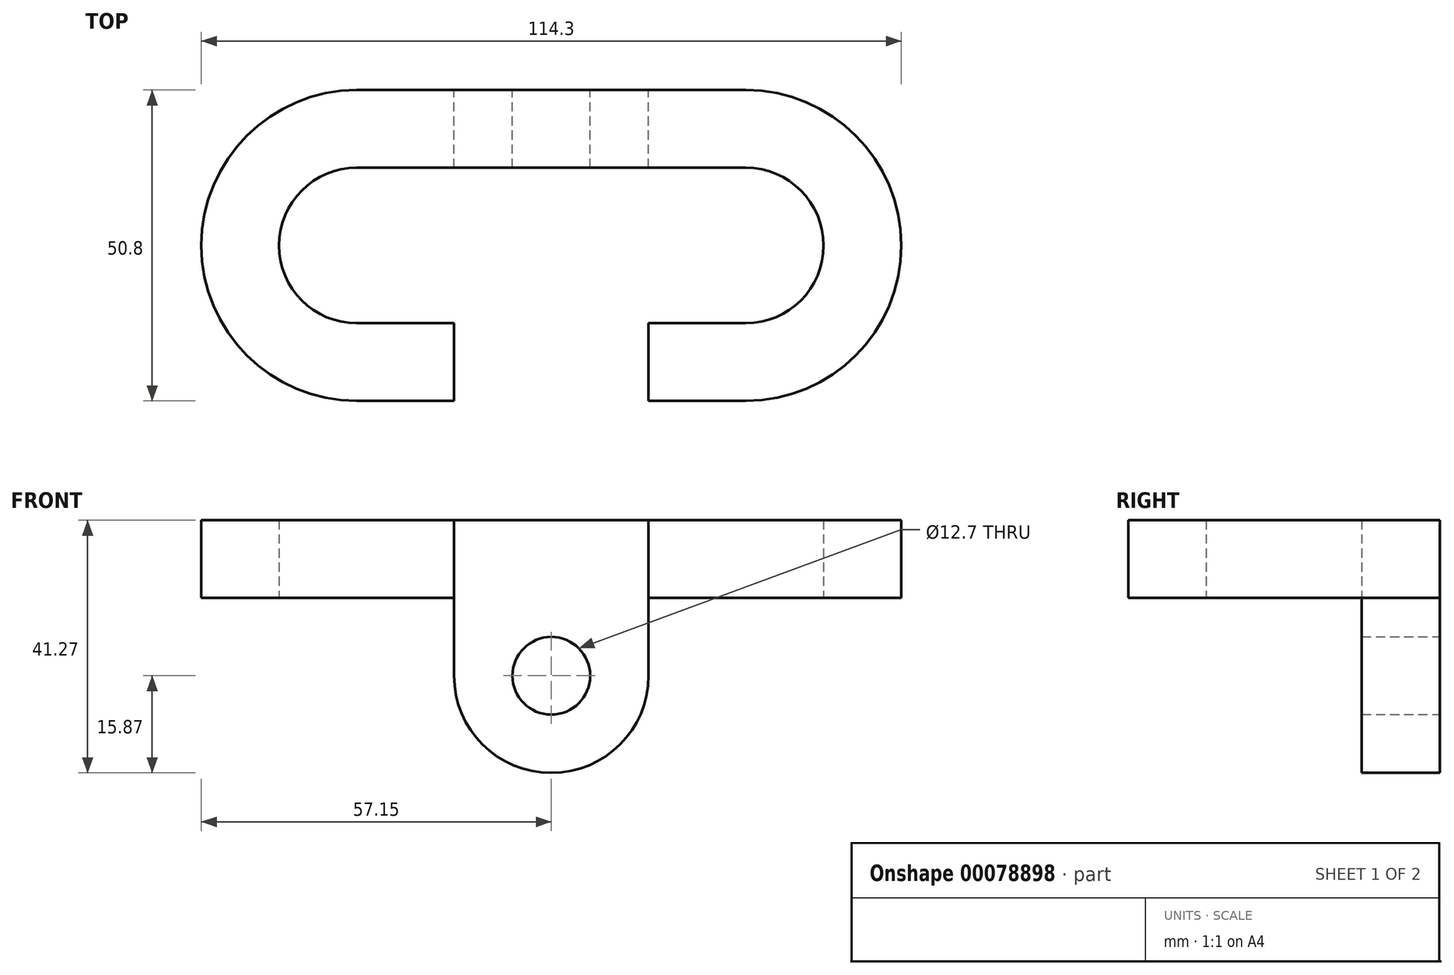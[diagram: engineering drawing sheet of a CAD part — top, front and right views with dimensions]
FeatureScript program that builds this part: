
annotation { "Feature Type Name" : "Feature", "Feature Type Description" : "" }
export const myFeature = defineFeature(function(context is Context, id is Id, definition is map)
    precondition{}
    {
        {
            var Q0;
            Q0=qCreatedBy(makeId("Top.planeOp"),FACE);
            var sketch = newSketch(context, id + "F0", { "sketchPlane" : qUnion([Q0])});
            skCircle(sketch, "E0", {"center": v(0, 0) * mm, "radius": 25.4 * mm});
            skCircle(sketch, "E1", {"center": v(63.5, 0) * mm, "radius": 25.4 * mm});
            skCircle(sketch, "E2", {"center": v(0, 0) * mm, "radius": 12.7 * mm});
            skCircle(sketch, "E3", {"center": v(63.5, 0) * mm, "radius": 12.7 * mm});
            skLineSegment(sketch, "E4", {"start": v(0, 25.4) * mm, "end": v(63.5, 25.4) * mm});
            skLineSegment(sketch, "E5", {"start": v(63.5, 12.7) * mm, "end": v(0, 12.7) * mm});
            skLineSegment(sketch, "E6", {"start": v(0, -25.4) * mm, "end": v(15.88, -25.4) * mm});
            skLineSegment(sketch, "E7", {"start": v(15.88, -25.4) * mm, "end": v(15.88, -12.7) * mm});
            skLineSegment(sketch, "E8", {"start": v(15.88, -12.7) * mm, "end": v(0, -12.7) * mm});
            skLineSegment(sketch, "E9", {"start": v(63.5, -12.7) * mm, "end": v(47.63, -12.7) * mm});
            skLineSegment(sketch, "E10", {"start": v(47.63, -12.7) * mm, "end": v(47.63, -25.4) * mm});
            skLineSegment(sketch, "E11", {"start": v(47.63, -25.4) * mm, "end": v(63.5, -25.4) * mm});
            skLineSegment(sketch, "E12", {"start": v(63.5, -25.4) * mm, "end": v(63.5, -12.7) * mm});
            skSolve(sketch);
        }
        {
            var Q0;
            {var subQ3=sQuery(id+"F0.wireOp",EDGE,"E8");Q0=makeQuery(id+"F0.imprint","IMPRINT",FACE,{"disambiguationData":[TD([[makeQuery(id+"F0.imprint","IMPRINT",EDGE,{"derivedFrom":subQ3}),1.0]])]});}
            var Q1;
            {var subQ0=sQuery(id+"F0.wireOp",EDGE,"E4");Q1=makeQuery(id+"F0.imprint","IMPRINT",FACE,{"disambiguationData":[TD([[makeQuery(id+"F0.imprint","IMPRINT",EDGE,{"derivedFrom":subQ0}),-1.0]])]});}
            var Q2;
            {var subQ5=sQuery(id+"F0.wireOp",EDGE,"E12");Q2=makeQuery(id+"F0.imprint","IMPRINT",FACE,{"disambiguationData":[TD([[makeQuery(id+"F0.imprint","IMPRINT",EDGE,{"derivedFrom":subQ5}),-1.0]])]});}
            var Q3;
            {var subQ0=sQuery(id+"F0.wireOp",EDGE,"E11");Q3=makeQuery(id+"F0.imprint","IMPRINT",FACE,{"disambiguationData":[TD([[makeQuery(id+"F0.imprint","IMPRINT",EDGE,{"derivedFrom":subQ0}),1.0]])]});}
            var Q4;
            {var subQ0=sQuery(id+"F0.wireOp",EDGE,"E6");Q4=makeQuery(id+"F0.imprint","IMPRINT",FACE,{"disambiguationData":[TD([[makeQuery(id+"F0.imprint","IMPRINT",EDGE,{"derivedFrom":subQ0}),1.0]])]});}
            var Q5;
            {var subQ4=sQuery(id+"F0.wireOp",EDGE,"E9");Q5=makeQuery(id+"F0.imprint","IMPRINT",FACE,{"disambiguationData":[TD([[makeQuery(id+"F0.imprint","IMPRINT",EDGE,{"derivedFrom":subQ4}),1.0]])]});}
            extrude(context, id + "F1", {"entities" : qUnion([Q0, Q1, Q2, Q3, Q4, Q5]), "depth" : 12.7 * mm});
        }
        {
            var Q0;
            Q0=makeQuery(id+"F1.opExtrude","SWEPT_FACE",FACE,{"disambiguationData":[OSD([sQuery(id+"F0.wireOp",EDGE,"E4")])]});
            var sketch = newSketch(context, id + "F2", { "sketchPlane" : qUnion([Q0])});
            skPoint(sketch, "E13", {"position": v(-31.75, 0) * mm});
            skCircle(sketch, "E14", {"center": v(-31.75, -12.7) * mm, "radius": 15.88 * mm});
            skLineSegment(sketch, "E15", {"start": v(-15.88, -12.7) * mm, "end": v(-15.88, 0) * mm});
            skLineSegment(sketch, "E16", {"start": v(-47.62, -12.7) * mm, "end": v(-47.62, 0) * mm});
            skCircle(sketch, "E17", {"center": v(-31.75, -12.7) * mm, "radius": 6.35 * mm});
            skSolve(sketch);
        }
        {
            var Q0;
            Q0 = qSketchRegion(id + "F2", true);
            var Q1;
            {var subQ0=sQuery(id+"F2.wireOp",EDGE,"E15");Q1=makeQuery(id+"F2.imprint","IMPRINT",FACE,{"disambiguationData":[TD([[makeQuery(id+"F2.imprint","IMPRINT",EDGE,{"derivedFrom":subQ0}),1.0]])]});}
            var Q2;
            {var subQ0=sQuery(id+"F2.wireOp",EDGE,"E16");Q2=makeQuery(id+"F2.imprint","IMPRINT",FACE,{"disambiguationData":[TD([[makeQuery(id+"F2.imprint","IMPRINT",EDGE,{"derivedFrom":subQ0}),-1.0]])]});}
            var Q3;
            Q3=makeQuery(id+"F1.opExtrude","SWEPT_FACE",FACE,{"disambiguationData":[OSD([sQuery(id+"F0.wireOp",EDGE,"E5")])]});
            extrude(context, id + "F3", {"entities" : qUnion([Q0, Q1, Q2]), "operationType" : NewBodyOperationType.ADD, "endBound" : BoundingType.UP_TO_SURFACE, "oppositeDirection" : true, "endBoundEntityFace" : qUnion([Q3]), "depth" : 25.4 * mm});
        }
    });
